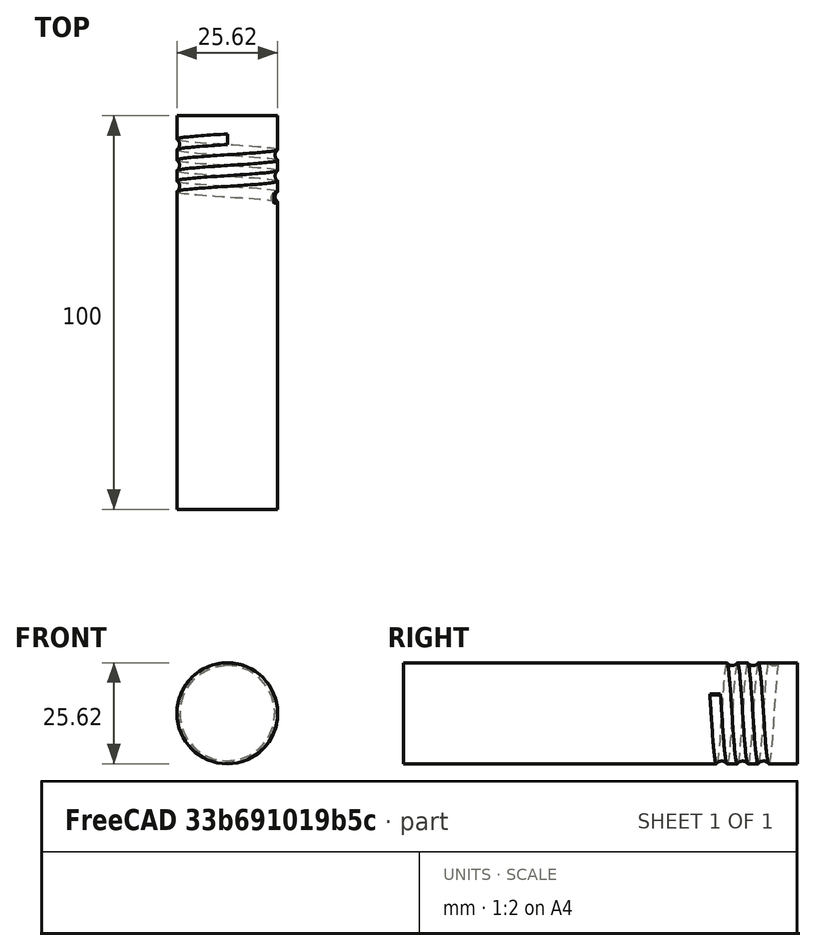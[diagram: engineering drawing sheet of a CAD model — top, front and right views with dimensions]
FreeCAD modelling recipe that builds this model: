
FCSTD DOCUMENT  (FreeCAD 0.21R33771 (Git))
Label: thread2
License: All rights reserved
LicenseURL: http://en.wikipedia.org/wiki/All_rights_reserved
objects: Sketcher::SketchObject×2, PartDesign::AdditiveHelix×1, PartDesign::Body×1, PartDesign::Pad×1, Part::Cut×1
note: 8 computed .brp shape members not serialized (recipe doc carries the construction recipe); baked Part::Feature solids carry a one-line shape summary decoded from their .brp

FEATURE [Sketcher::SketchObject] Sketch001
  FullyConstrained = false
  MapMode = 5
  Placement = pos=(0,0,0) rot=(0.57735,0.57735,0.57735;2.0944rad)
  Support = -> [YZ_Plane]
  sketch-geometry (1):
    g0: Circle CenterX=-5.95857 CenterY=13.8368 CenterZ=0 NormalX=0 NormalY=0 NormalZ=1 AngleXU=0 Radius=1.70515
FEATURE [PartDesign::AdditiveHelix] AdditiveHelix
  Angle = 0
  Axis = (1e-16,1,-1e-16)
  Base = (0,0,0)
  Growth = 0
  HasBeenEdited = true
  Height = 14.92
  LeftHanded = false
  Mode = 0
  Outside = false
  Pitch = 5.30517
  Placement = pos=(0,0,0) rot=(1,1,1;2.0944rad)
  Profile = -> Sketch001
  ReferenceAxis = -> Y_Axis
  Refine = true
  Reversed = true
  Turns = 2.81235
FEATURE [Sketcher::SketchObject] Sketch
  FullyConstrained = false
  MapMode = 5
  Placement = pos=(0,0,0) rot=(1,0,0;1.5708rad)
  Support = -> [XZ_Plane]
  sketch-geometry (1):
    g0: Circle CenterX=0 CenterY=0 CenterZ=0 NormalX=0 NormalY=0 NormalZ=1 AngleXU=0 Radius=12.8071
  constraints (1):
    c: Coincident(g0,g-1)
FEATURE [PartDesign::Body] Body
  Group = -> [Sketch,Sketch001]
  Origin = -> Origin
FEATURE [PartDesign::Pad] Pad
  Direction = (0,-1,2e-16)
  Length = 100
  Length2 = 10
  Placement = pos=(0,0,0) rot=(1,0,0;1.5708rad)
  Profile = -> Sketch
  ReferenceAxis = -> Sketch [N_Axis]
  Refine = true
  Type = 0
FEATURE [Part::Cut] Cut
  Base = -> Pad
  Refine = true
  Tool = -> AdditiveHelix
